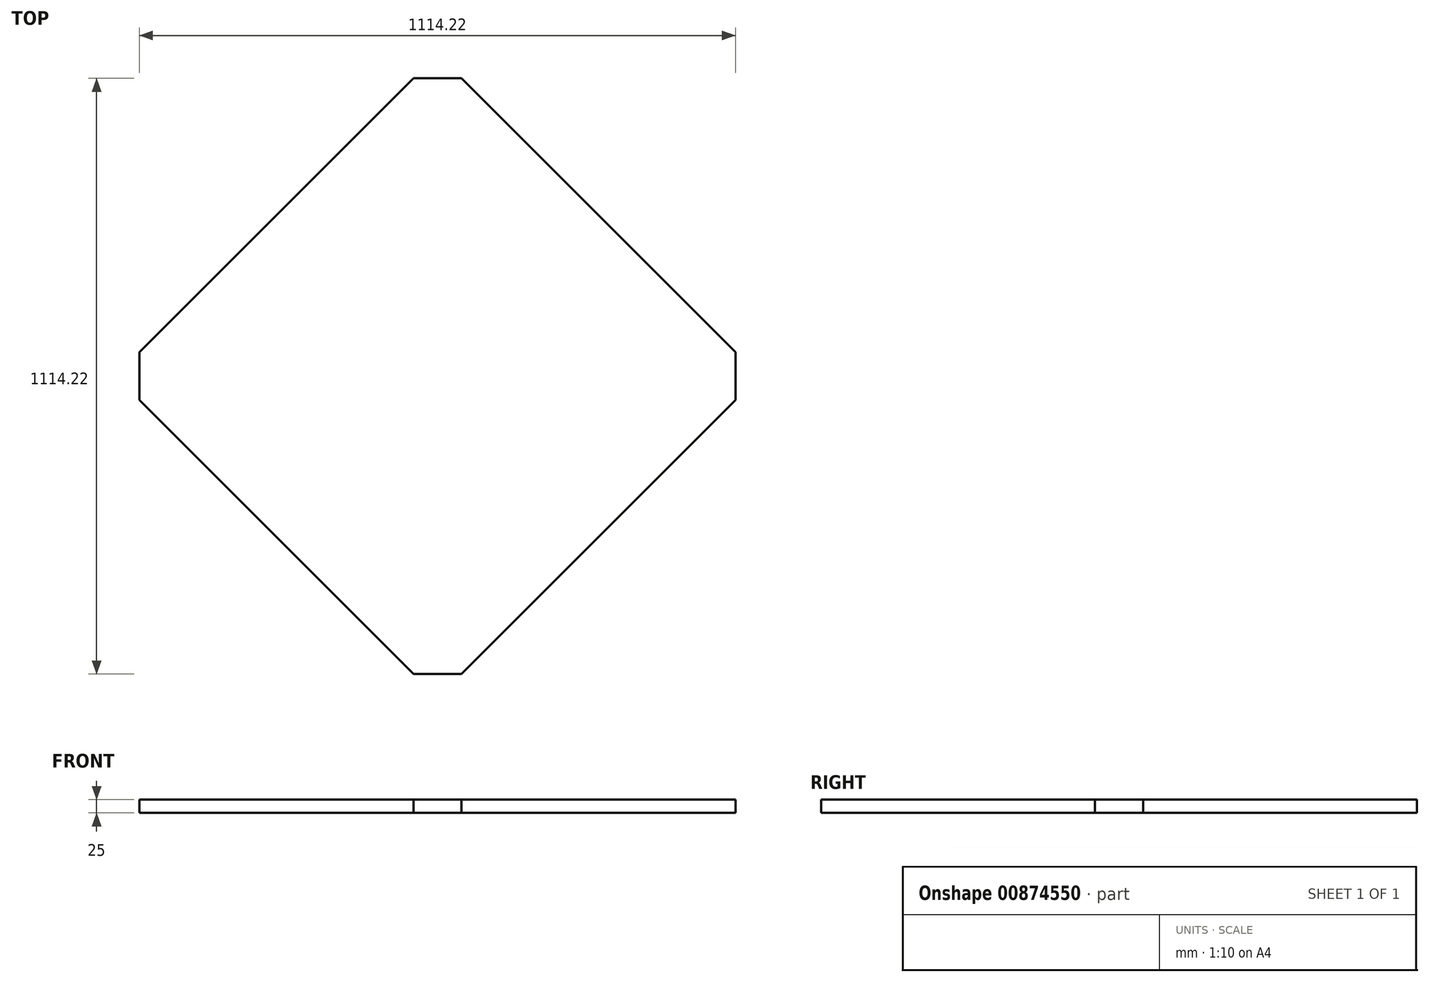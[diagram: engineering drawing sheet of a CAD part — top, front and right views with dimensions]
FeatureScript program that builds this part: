
annotation { "Feature Type Name" : "Feature", "Feature Type Description" : "" }
export const myFeature = defineFeature(function(context is Context, id is Id, definition is map)
    precondition{}
    {
        {
            var Q0;
            Q0=qCreatedBy(makeId("Top.planeOp"),FACE);
            var sketch = newSketch(context, id + "F0", { "sketchPlane" : qUnion([Q0])});
            skLineSegment(sketch, "E0.bottom", {"start": v(512.11, 0) * mm, "end": v(602.11, 0) * mm});
            skLineSegment(sketch, "E0.top", {"start": v(512.11, 1114.22) * mm, "end": v(602.11, 1114.22) * mm});
            skLineSegment(sketch, "E0.left", {"start": v(0, 512.11) * mm, "end": v(0, 602.11) * mm});
            skLineSegment(sketch, "E0.right", {"start": v(1114.22, 512.11) * mm, "end": v(1114.22, 602.11) * mm});
            skCircle(sketch, "E1", {"center": v(0, 557.11) * mm, "radius": 45 * mm, "construction": true});
            skLineSegment(sketch, "E2", {"start": v(0, 602.11) * mm, "end": v(512.11, 1114.22) * mm});
            skLineSegment(sketch, "E3", {"start": v(0, 512.11) * mm, "end": v(512.11, 0) * mm});
            skLineSegment(sketch, "E4", {"start": v(557.11, 0) * mm, "end": v(557.11, -37.7) * mm, "construction": true});
            skLineSegment(sketch, "E5.MirrorCS", {"start": v(1114.22, 512.11) * mm, "end": v(602.11, 0) * mm});
            skLineSegment(sketch, "E6.MirrorCS", {"start": v(1114.22, 602.11) * mm, "end": v(602.11, 1114.22) * mm});
            skPoint(sketch, "E7.orphan", {"position": v(516.1, -4) * mm});
            skPoint(sketch, "E8.orphan", {"position": v(598.12, -4) * mm});
            skPoint(sketch, "E9.orphan", {"position": v(1114.22, 0) * mm});
            skPoint(sketch, "E10.orphan", {"position": v(0, 1114.22) * mm});
            skPoint(sketch, "E11.orphan", {"position": v(0, 0) * mm});
            skPoint(sketch, "E12.orphan", {"position": v(536.53, 1138.64) * mm});
            skPoint(sketch, "E13.orphan", {"position": v(577.7, 1138.64) * mm});
            skSolve(sketch);
        }
        {
            var Q0;
            Q0=makeQuery(id+"F0.imprint","IMPRINT",FACE,{"disambiguationData":[TD([[makeQuery(id+"F0.imprint","IMPRINT",EDGE,{"derivedFrom":sQuery(id+"F0.wireOp",EDGE,"E0.bottom")}),1.0]])]});
            extrude(context, id + "F1", {"entities" : qUnion([Q0]), "depth" : 25 * mm, "offsetDistance" : 25 * mm});
        }
    });
